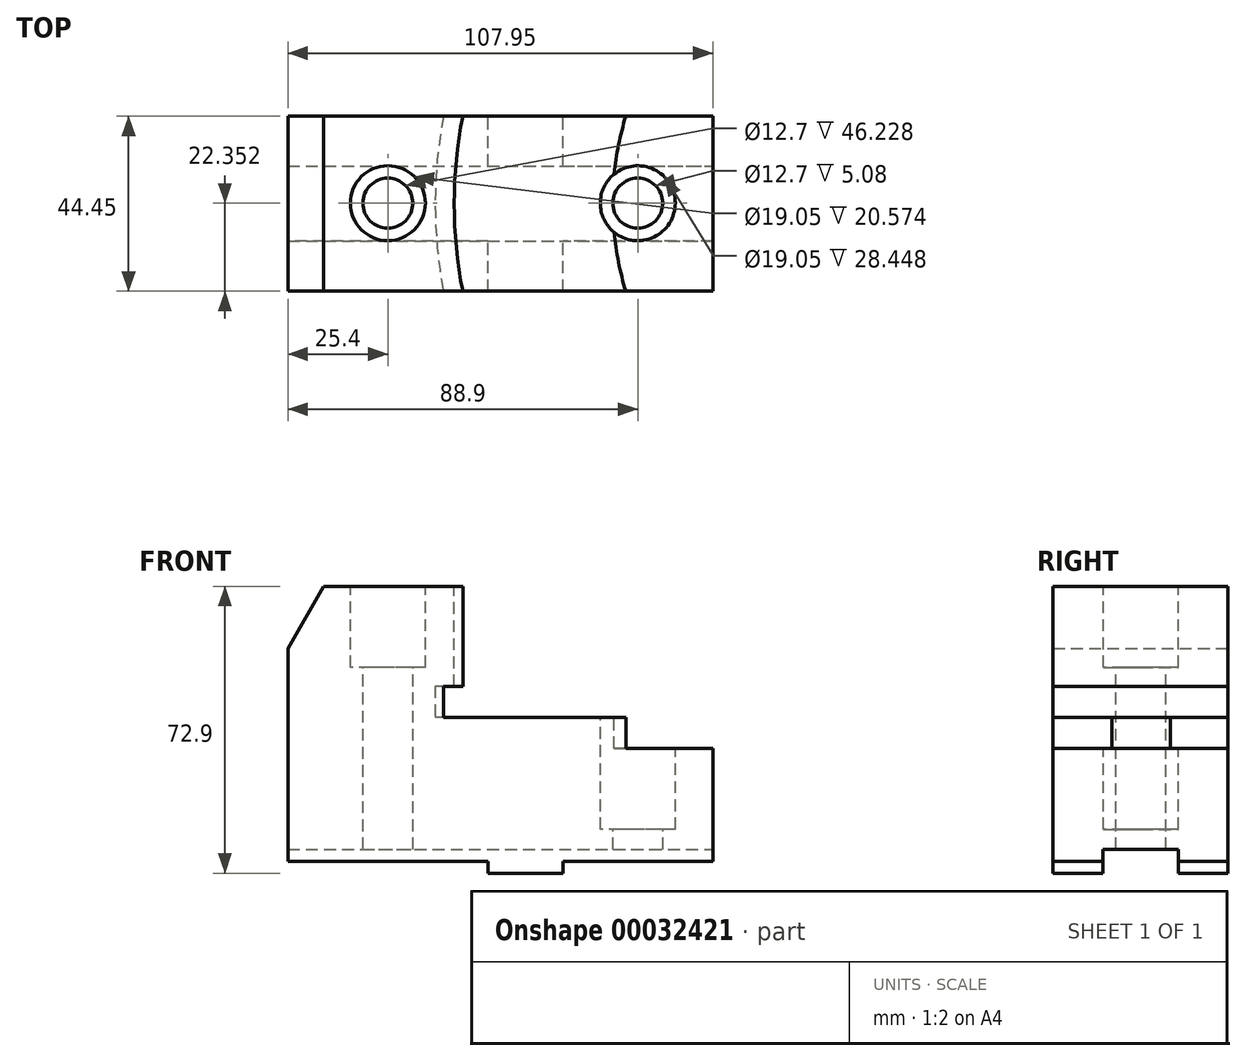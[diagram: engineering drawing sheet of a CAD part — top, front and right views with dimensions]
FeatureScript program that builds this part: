
annotation { "Feature Type Name" : "Feature", "Feature Type Description" : "" }
export const myFeature = defineFeature(function(context is Context, id is Id, definition is map)
    precondition{}
    {
        {
            var Q0;
            Q0=qCreatedBy(makeId("Front.planeOp"),FACE);
            var sketch = newSketch(context, id + "F0", { "sketchPlane" : qUnion([Q0])});
            skLineSegment(sketch, "E0", {"start": v(0, 0) * mm, "end": v(0, 69.85) * mm});
            skLineSegment(sketch, "E1", {"start": v(0, 69.85) * mm, "end": v(44.45, 69.85) * mm});
            skLineSegment(sketch, "E2", {"start": v(44.45, 69.85) * mm, "end": v(44.45, 36.58) * mm});
            skLineSegment(sketch, "E3", {"start": v(44.45, 36.58) * mm, "end": v(86.02, 36.58) * mm});
            skLineSegment(sketch, "E4", {"start": v(86.02, 36.58) * mm, "end": v(86.02, 28.7) * mm});
            skLineSegment(sketch, "E5", {"start": v(86.02, 28.7) * mm, "end": v(107.95, 28.7) * mm});
            skLineSegment(sketch, "E6", {"start": v(107.95, 28.7) * mm, "end": v(107.95, 0) * mm});
            skLineSegment(sketch, "E7", {"start": v(107.95, 0) * mm, "end": v(69.85, 0) * mm});
            skLineSegment(sketch, "E8", {"start": v(69.85, 0) * mm, "end": v(69.85, -3.05) * mm});
            skLineSegment(sketch, "E9", {"start": v(69.85, -3.05) * mm, "end": v(50.83, -3.05) * mm});
            skLineSegment(sketch, "E10", {"start": v(50.83, -3.05) * mm, "end": v(50.83, 0) * mm});
            skLineSegment(sketch, "E11", {"start": v(50.83, 0) * mm, "end": v(0, 0) * mm});
            skSolve(sketch);
        }
        {
            var Q0;
            Q0=makeQuery(id+"F0.imprint","IMPRINT",FACE,{"disambiguationData":[TD([[makeQuery(id+"F0.imprint","IMPRINT",EDGE,{"derivedFrom":sQuery(id+"F0.wireOp",EDGE,"E0")}),-1.0]])]});
            extrude(context, id + "F1", {"entities" : qUnion([Q0]), "depth" : 44.45 * mm});
        }
        {
            var Q0;
            Q0=makeQuery(id+"F1.opExtrude","SWEPT_FACE",FACE,{"disambiguationData":[OSD([sQuery(id+"F0.wireOp",EDGE,"E3")])]});
            var sketch = newSketch(context, id + "F2", { "sketchPlane" : qUnion([Q0])});
            skArc(sketch, "E12", {"start": v(85.86, 0) * mm, "mid": v(82.55, -22.23) * mm, "end": v(85.86, -44.45) * mm});
            skLineSegment(sketch, "E13", {"start": v(158.75, -22.22) * mm, "end": v(107.95, -22.22) * mm, "construction": true});
            skSolve(sketch);
        }
        {
            var Q0;
            {var subQ2=sQuery(id+"F2.wireOp",EDGE,"E12");Q0=makeQuery(id+"F2.imprint","IMPRINT",FACE,{"disambiguationData":[TD([[makeQuery(id+"F2.imprint","IMPRINT",EDGE,{"derivedFrom":subQ2}),1.0]])]});}
            var Q1;
            Q1=makeQuery(id+"F1.opExtrude","SWEPT_FACE",FACE,{"disambiguationData":[OSD([sQuery(id+"F0.wireOp",EDGE,"E5")])]});
            extrude(context, id + "F3", {"entities" : qUnion([Q0]), "operationType" : NewBodyOperationType.REMOVE, "endBound" : BoundingType.UP_TO_SURFACE, "oppositeDirection" : true, "endBoundEntityFace" : qUnion([Q1]), "depth" : 25.4 * mm});
        }
        {
            var Q0;
            Q0=makeQuery(id+"F1.opExtrude","SWEPT_FACE",FACE,{"disambiguationData":[OSD([sQuery(id+"F0.wireOp",EDGE,"E1")])]});
            var sketch = newSketch(context, id + "F4", { "sketchPlane" : qUnion([Q0])});
            skArc(sketch, "E14", {"start": v(44.45, 0) * mm, "mid": v(42.27, -22.23) * mm, "end": v(44.45, -44.45) * mm});
            skSolve(sketch);
        }
        {
            var Q0;
            Q0=makeQuery(id+"F4.imprint","IMPRINT",FACE,{"disambiguationData":[TD([[makeQuery(id+"F4.imprint","IMPRINT",EDGE,{"derivedFrom":sQuery(id+"F4.wireOp",EDGE,"E14")}),1.0]])]});
            var Q1;
            Q1=makeQuery(id+"F1.opExtrude","SWEPT_FACE",FACE,{"disambiguationData":[OSD([sQuery(id+"F0.wireOp",EDGE,"E3")])]});
            extrude(context, id + "F5", {"entities" : qUnion([Q0]), "operationType" : NewBodyOperationType.REMOVE, "endBound" : BoundingType.UP_TO_SURFACE, "oppositeDirection" : true, "endBoundEntityFace" : qUnion([Q1]), "depth" : 25.4 * mm});
        }
        {
            var Q0;
            Q0=makeQuery(id+"F5.boolean.opBoolean","MERGE",FACE,{"derivedFrom":[makeQuery(id+"F1.opExtrude","SWEPT_FACE",FACE,{"disambiguationData":[OSD([sQuery(id+"F0.wireOp",EDGE,"E3")])]}),makeQuery(id+"F5.opExtrude","CAP_FACE",FACE,{"disambiguationData":[OSD([sQuery(id+"F0.wireOp",EDGE,"E1"),sQuery(id+"F0.wireOp",EDGE,"E2"),sQuery(id+"F4.wireOp",EDGE,"E14")])],"isStart":false})]});
            var sketch = newSketch(context, id + "F6", { "sketchPlane" : qUnion([Q0])});
            skArc(sketch, "E15", {"start": v(39.53, 0) * mm, "mid": v(37.44, -22.23) * mm, "end": v(39.53, -44.45) * mm});
            skLineSegment(sketch, "E16", {"start": v(39.53, 0) * mm, "end": v(44.45, 0) * mm});
            skLineSegment(sketch, "E17", {"start": v(39.53, -44.45) * mm, "end": v(44.45, -44.45) * mm});
            skSolve(sketch);
        }
        {
            var Q0;
            Q0=makeQuery(id+"F6.imprint","IMPRINT",FACE,{"disambiguationData":[TD([[makeQuery(id+"F6.imprint","IMPRINT",EDGE,{"derivedFrom":sQuery(id+"F6.wireOp",EDGE,"E15")}),1.0]])]});
            var Q1;
            Q1=makeQuery(id+"F1.opExtrude","SWEPT_FACE",FACE,{"disambiguationData":[OSD([sQuery(id+"F0.wireOp",EDGE,"E1")])]});
            extrude(context, id + "F7", {"entities" : qUnion([Q0]), "operationType" : NewBodyOperationType.REMOVE, "endBoundEntityFace" : qUnion([Q1]), "depth" : 7.87 * mm});
        }
        {
            var Q0;
            Q0=makeQuery(id+"F1.opExtrude","SWEPT_FACE",FACE,{"disambiguationData":[OSD([sQuery(id+"F0.wireOp",EDGE,"E1")])]});
            var sketch = newSketch(context, id + "F8", { "sketchPlane" : qUnion([Q0])});
            skPoint(sketch, "E18", {"position": v(25.4, -22.1) * mm});
            skSolve(sketch);
        }
        {
            var Q0;
            Q0=sQuery(id+"F8.wireOp",VERTEX,"E18");
            var Q1;
            Q1=makeQuery(id+"F1.opExtrude","SWEPT_BODY",BODY,{"disambiguationData":[OSD([sQuery(id+"F0.wireOp",EDGE,"E0"),sQuery(id+"F0.wireOp",EDGE,"E1"),sQuery(id+"F0.wireOp",EDGE,"E2"),sQuery(id+"F0.wireOp",EDGE,"E3"),sQuery(id+"F0.wireOp",EDGE,"E4"),sQuery(id+"F0.wireOp",EDGE,"E5"),sQuery(id+"F0.wireOp",EDGE,"E6"),sQuery(id+"F0.wireOp",EDGE,"E7"),sQuery(id+"F0.wireOp",EDGE,"E8"),sQuery(id+"F0.wireOp",EDGE,"E9"),sQuery(id+"F0.wireOp",EDGE,"E10"),sQuery(id+"F0.wireOp",EDGE,"E11")])]});
            hole(context, id + "F9", {"style" : HoleStyle.C_BORE, "holeDiameter" : 12.7 * mm, "cBoreDiameter" : 19.05 * mm, "cBoreDepth" : 20.57 * mm, "endStyle" : HoleEndStyle.THROUGH, "locations" : qUnion([Q0]), "scope" : qUnion([Q1])});
        }
        {
            var Q0;
            {var subQ0=sQuery(id+"F4.wireOp",EDGE,"E14");Q0=makeQuery(id+"F7.boolean.opBoolean","MERGE",FACE,{"derivedFrom":[makeQuery(id+"F5.boolean.opBoolean","MERGE",FACE,{"derivedFrom":[makeQuery(id+"F1.opExtrude","SWEPT_FACE",FACE,{"disambiguationData":[OSD([sQuery(id+"F0.wireOp",EDGE,"E3")])]}),makeQuery(id+"F5.opExtrude","CAP_FACE",FACE,{"disambiguationData":[OSD([sQuery(id+"F0.wireOp",EDGE,"E1"),sQuery(id+"F0.wireOp",EDGE,"E2"),subQ0])],"isStart":false})]}),makeQuery(id+"F7.opExtrude","CAP_FACE",FACE,{"disambiguationData":[OSD([subQ0,sQuery(id+"F6.wireOp",EDGE,"E15"),sQuery(id+"F6.wireOp",EDGE,"E16"),sQuery(id+"F6.wireOp",EDGE,"E17")])],"isStart":true})]});}
            var sketch = newSketch(context, id + "F10", { "sketchPlane" : qUnion([Q0])});
            skPoint(sketch, "E19", {"position": v(88.9, -22.1) * mm});
            skSolve(sketch);
        }
        {
            var Q0;
            Q0=sQuery(id+"F10.wireOp",VERTEX,"E19");
            var Q1;
            Q1=makeQuery(id+"F1.opExtrude","SWEPT_BODY",BODY,{"disambiguationData":[OSD([sQuery(id+"F0.wireOp",EDGE,"E0"),sQuery(id+"F0.wireOp",EDGE,"E1"),sQuery(id+"F0.wireOp",EDGE,"E2"),sQuery(id+"F0.wireOp",EDGE,"E3"),sQuery(id+"F0.wireOp",EDGE,"E4"),sQuery(id+"F0.wireOp",EDGE,"E5"),sQuery(id+"F0.wireOp",EDGE,"E6"),sQuery(id+"F0.wireOp",EDGE,"E7"),sQuery(id+"F0.wireOp",EDGE,"E8"),sQuery(id+"F0.wireOp",EDGE,"E9"),sQuery(id+"F0.wireOp",EDGE,"E10"),sQuery(id+"F0.wireOp",EDGE,"E11")])]});
            hole(context, id + "F11", {"style" : HoleStyle.C_BORE, "holeDiameter" : 12.7 * mm, "cBoreDiameter" : 19.05 * mm, "cBoreDepth" : 20.57 * mm, "endStyle" : HoleEndStyle.THROUGH, "locations" : qUnion([Q0]), "scope" : qUnion([Q1])});
        }
        {
            var Q0;
            Q0=makeQuery(id+"F1.opExtrude","SWEPT_FACE",FACE,{"disambiguationData":[OSD([sQuery(id+"F0.wireOp",EDGE,"E6")])]});
            var sketch = newSketch(context, id + "F12", { "sketchPlane" : qUnion([Q0])});
            skLineSegment(sketch, "E20.top", {"start": v(-31.75, 3.05) * mm, "end": v(-12.65, 3.05) * mm});
            skLineSegment(sketch, "E21", {"start": v(-31.75, 3.05) * mm, "end": v(-31.75, -3.05) * mm});
            skLineSegment(sketch, "E22", {"start": v(-31.75, -3.05) * mm, "end": v(-12.65, -3.05) * mm});
            skLineSegment(sketch, "E23", {"start": v(-12.65, -3.05) * mm, "end": v(-12.65, 3.05) * mm});
            skSolve(sketch);
        }
        {
            var Q0;
            {var subQ5=sQuery(id+"F12.wireOp",EDGE,"E20.top");Q0=makeQuery(id+"F12.imprint","IMPRINT",FACE,{"disambiguationData":[TD([[makeQuery(id+"F12.imprint","IMPRINT",EDGE,{"derivedFrom":subQ5}),-1.0]])]});}
            var Q1;
            {var subQ5=sQuery(id+"F12.wireOp",EDGE,"E22");Q1=makeQuery(id+"F12.imprint","IMPRINT",FACE,{"disambiguationData":[TD([[makeQuery(id+"F12.imprint","IMPRINT",EDGE,{"derivedFrom":subQ5}),1.0]])]});}
            extrude(context, id + "F13", {"entities" : qUnion([Q0, Q1]), "operationType" : NewBodyOperationType.REMOVE, "endBound" : BoundingType.THROUGH_ALL, "oppositeDirection" : true, "depth" : 25.4 * mm});
        }
        {
            var Q0;
            Q0=makeQuery(id+"F1.opExtrude","SWEPT_EDGE",EDGE,{"disambiguationData":[OSD([sQuery(id+"F0.wireOp",EDGE,"E0"),sQuery(id+"F0.wireOp",EDGE,"E1")])]});
            chamfer(context, id + "F14", {"entities" : qUnion([Q0]), "chamferType" : ChamferType.OFFSET_ANGLE, "width" : 15.75 * mm, "oppositeDirection" : false, "angle" : 30 * degree, "tangentPropagation" : true});
        }
    });
